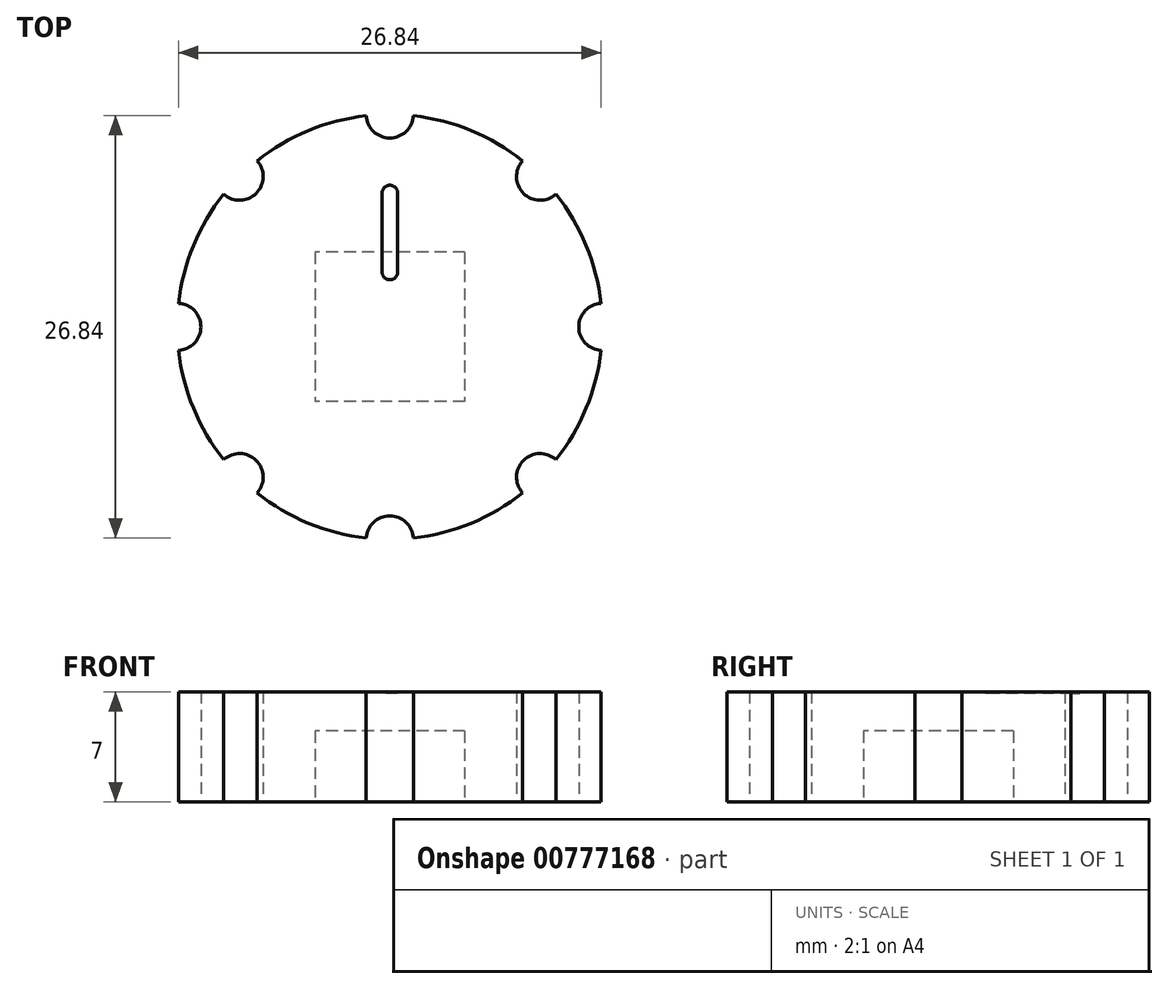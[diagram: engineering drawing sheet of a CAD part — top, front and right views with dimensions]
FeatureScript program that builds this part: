
annotation { "Feature Type Name" : "Feature", "Feature Type Description" : "" }
export const myFeature = defineFeature(function(context is Context, id is Id, definition is map)
    precondition{}
    {
        {
            var Q0;
            Q0=qCreatedBy(makeId("Top.planeOp"),FACE);
            var sketch = newSketch(context, id + "F0", { "sketchPlane" : qUnion([Q0])});
            skCircle(sketch, "E0", {"center": v(0, 0) * mm, "radius": 13.5 * mm});
            skSolve(sketch);
        }
        {
            var Q0;
            Q0=qSketchRegion(id+"F0",true);
            extrude(context, id + "F1", {"entities" : qUnion([Q0]), "depth" : 7 * mm, "offsetDistance" : 25.4 * mm});
        }
        {
            var Q0;
            Q0=qCreatedBy(makeId("Top.planeOp"),FACE);
            var sketch = newSketch(context, id + "F2", { "sketchPlane" : qUnion([Q0])});
            skLineSegment(sketch, "E1.bottom", {"start": v(4.75, 4.75) * mm, "end": v(-4.75, 4.75) * mm});
            skLineSegment(sketch, "E1.top", {"start": v(4.75, -4.75) * mm, "end": v(-4.75, -4.75) * mm});
            skLineSegment(sketch, "E1.left", {"start": v(4.75, 4.75) * mm, "end": v(4.75, -4.75) * mm});
            skLineSegment(sketch, "E1.right", {"start": v(-4.75, 4.75) * mm, "end": v(-4.75, -4.75) * mm});
            skPoint(sketch, "E1.middle", {"position": v(0, 0) * mm});
            skSolve(sketch);
        }
        {
            var Q0;
            Q0=qSketchRegion(id+"F2",true);
            extrude(context, id + "F3", {"entities" : qUnion([Q0]), "operationType" : NewBodyOperationType.REMOVE, "depth" : 4.5 * mm, "offsetDistance" : 25.4 * mm});
        }
        {
            var Q0;
            Q0=qCreatedBy(makeId("Top.planeOp"),FACE);
            var sketch = newSketch(context, id + "F4", { "sketchPlane" : qUnion([Q0])});
            skCircle(sketch, "E2", {"center": v(13.5, 0) * mm, "radius": 1.5 * mm});
            skCircle(sketch, "E3", {"center": v(-13.5, 0) * mm, "radius": 1.5 * mm});
            skCircle(sketch, "E4", {"center": v(0, -13.5) * mm, "radius": 1.5 * mm});
            skCircle(sketch, "E5.MirrorC", {"center": v(0, 13.5) * mm, "radius": 1.5 * mm});
            skLineSegment(sketch, "E6", {"start": v(-13.5, 13.5) * mm, "end": v(13.5, -13.5) * mm});
            skLineSegment(sketch, "E7.MirrorCS", {"start": v(13.5, 13.5) * mm, "end": v(-13.5, -13.5) * mm});
            skCircle(sketch, "E8", {"center": v(-9.55, -9.55) * mm, "radius": 1.5 * mm});
            skCircle(sketch, "E9.MirrorC", {"center": v(9.55, 9.55) * mm, "radius": 1.5 * mm});
            skCircle(sketch, "E10", {"center": v(9.55, -9.55) * mm, "radius": 1.5 * mm});
            skCircle(sketch, "E11.MirrorC", {"center": v(-9.55, 9.55) * mm, "radius": 1.5 * mm});
            skSolve(sketch);
        }
        {
            var Q0;
            Q0=qSketchRegion(id+"F4",true);
            extrude(context, id + "F5", {"entities" : qUnion([Q0]), "operationType" : NewBodyOperationType.REMOVE, "depth" : 25.4 * mm, "offsetDistance" : 25.4 * mm});
        }
        {
            var Q0;
            Q0=qCreatedBy(makeId("Top.planeOp"),FACE);
            cPlane(context, id + "F6", {"entities" : qUnion([Q0]), "cplaneType" : CPlaneType.OFFSET, "offset" : 7 * mm, "width" : 152.4 * mm, "height" : 152.4 * mm});
        }
        {
            var Q0;
            Q0=qCreatedBy(id+"F6.planeOp",FACE);
            var sketch = newSketch(context, id + "F7", { "sketchPlane" : qUnion([Q0])});
            skLineSegment(sketch, "E12.bottom", {"start": v(0.5, 8.5) * mm, "end": v(-0.5, 8.5) * mm});
            skLineSegment(sketch, "E12.top", {"start": v(0.5, 3.5) * mm, "end": v(-0.5, 3.5) * mm});
            skLineSegment(sketch, "E12.left", {"start": v(0.5, 8.5) * mm, "end": v(0.5, 3.5) * mm});
            skLineSegment(sketch, "E12.right", {"start": v(-0.5, 8.5) * mm, "end": v(-0.5, 3.5) * mm});
            skPoint(sketch, "E12.middle", {"position": v(0, 6) * mm});
            skCircle(sketch, "E13", {"center": v(0, 8.5) * mm, "radius": 0.5 * mm});
            skCircle(sketch, "E14", {"center": v(0, 3.5) * mm, "radius": 0.5 * mm});
            skSolve(sketch);
        }
        {
            var Q0;
            Q0=qSketchRegion(id+"F7",true);
            extrude(context, id + "F8", {"entities" : qUnion([Q0]), "operationType" : NewBodyOperationType.REMOVE, "oppositeDirection" : true, "depth" : 0.1 * mm, "offsetDistance" : 25.4 * mm});
        }
    });
